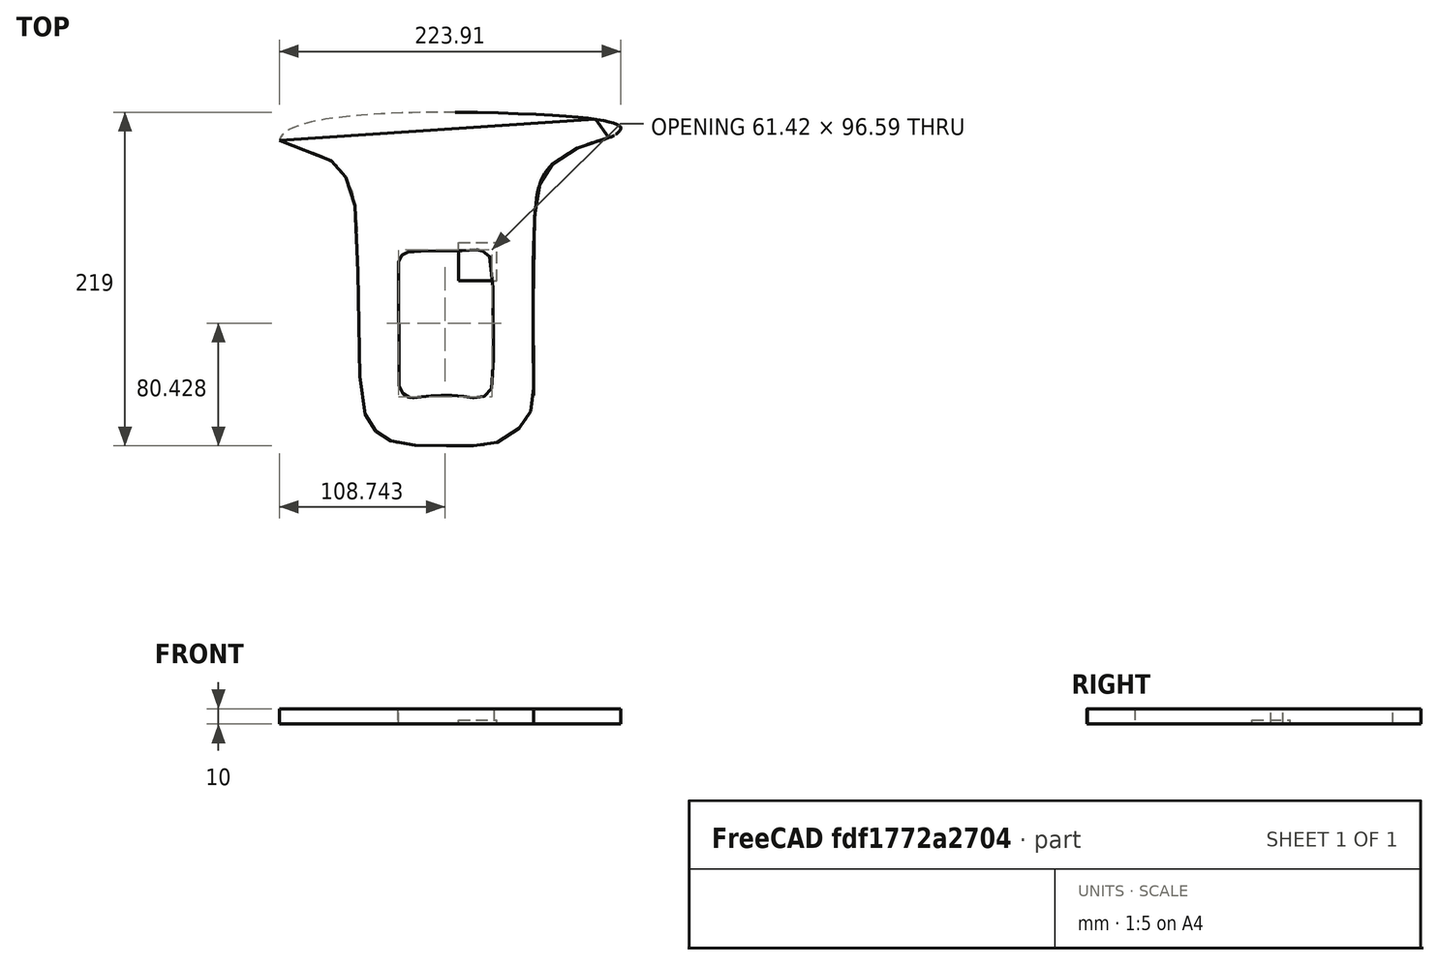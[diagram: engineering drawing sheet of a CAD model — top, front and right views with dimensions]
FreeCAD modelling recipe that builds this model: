
FCSTD DOCUMENT  (FreeCAD 0.19R)
Label: seatbelt
License: All rights reserved
LicenseURL: http://en.wikipedia.org/wiki/All_rights_reserved
objects: Mesh::Feature×2, Image::ImagePlane×1, Sketcher::SketchObject×1, PartDesign::Pad×1, PartDesign::Body×1, Part::Box×1
note: 5 computed .brp shape members not serialized (recipe doc carries the construction recipe); baked Part::Feature solids carry a one-line shape summary decoded from their .brp

FEATURE [Image::ImagePlane] ImagePlane
  XSize = 238
  YSize = 280
FEATURE [Sketcher::SketchObject] Sketch
  FullyConstrained = false
  MapMode = 5
  Support = -> [XY_Plane]
  sketch-geometry (166):
    g0-g32: Circle x33 (B-spline internal-alignment scaffolding for g33; pole/knot coordinates omitted)
    g33: BSplineCurve PolesCount=33 KnotsCount=31 Degree=3 IsPeriodic=0
    g34-g64: GeomPoint x31 (B-spline internal-alignment scaffolding for g33; pole/knot coordinates omitted)
    g65-g115: Circle x51 (B-spline internal-alignment scaffolding for g116; pole/knot coordinates omitted)
    g116: BSplineCurve PolesCount=51 KnotsCount=49 Degree=3 IsPeriodic=0
    g117-g165: GeomPoint x49 (B-spline internal-alignment scaffolding for g116; pole/knot coordinates omitted)
  constraints (24):
    c: Weight(g0) = 1
    c: Equal(g0, g1-g32) x32
    c: Coincident(g32,g0)
    c: InternalAlignment(g0-g32 -> g33) x33
    c: InternalAlignment(g34-g64 -> g33) x31
    c: Weight(g65) = 1
    c: Equal(g65, g66-g73) x8
    c: PointOnObject(g73,g72)
    c: Equal(g65,g74)
    c: PointOnObject(g74,g73)
    c: Equal(g65, g75-g84) x10
    c: PointOnObject(g84,g-2)
    c: Equal(g65,g85)
    c: Equal(g65,g86)
    c: Equal(g65,g87)
    c: PointOnObject(g87,g86)
    c: Equal(g65, g88-g101) x14
    c: PointOnObject(g101,g100)
    c: Equal(g65, g102-g114) x13
    c: PointOnObject(g116,g113)
    c: Equal(g65,g115)
    c: Coincident(g115,g65)
    c: InternalAlignment(g65-g115 -> g116) x51
    c: InternalAlignment(g117-g165 -> g116) x49
FEATURE [PartDesign::Pad] Pad
  Direction = (1,1,1)
  Length = 10
  Length2 = 100
  Profile = -> Sketch
  Type = 0
FEATURE [PartDesign::Body] Body
  Group = -> [Sketch,Pad]
  Origin = -> Origin
  Tip = -> Pad
FEATURE [Mesh::Feature] Mesh  label="Pad (Meshed)"
FEATURE [Part::Box] Box  label="Cube"
  AttacherType = Attacher::AttachEngine3D
  Height = 2.6
  Length = 25
  Width = 25
FEATURE [Mesh::Feature] Mesh001  label="Cube (Meshed)"
